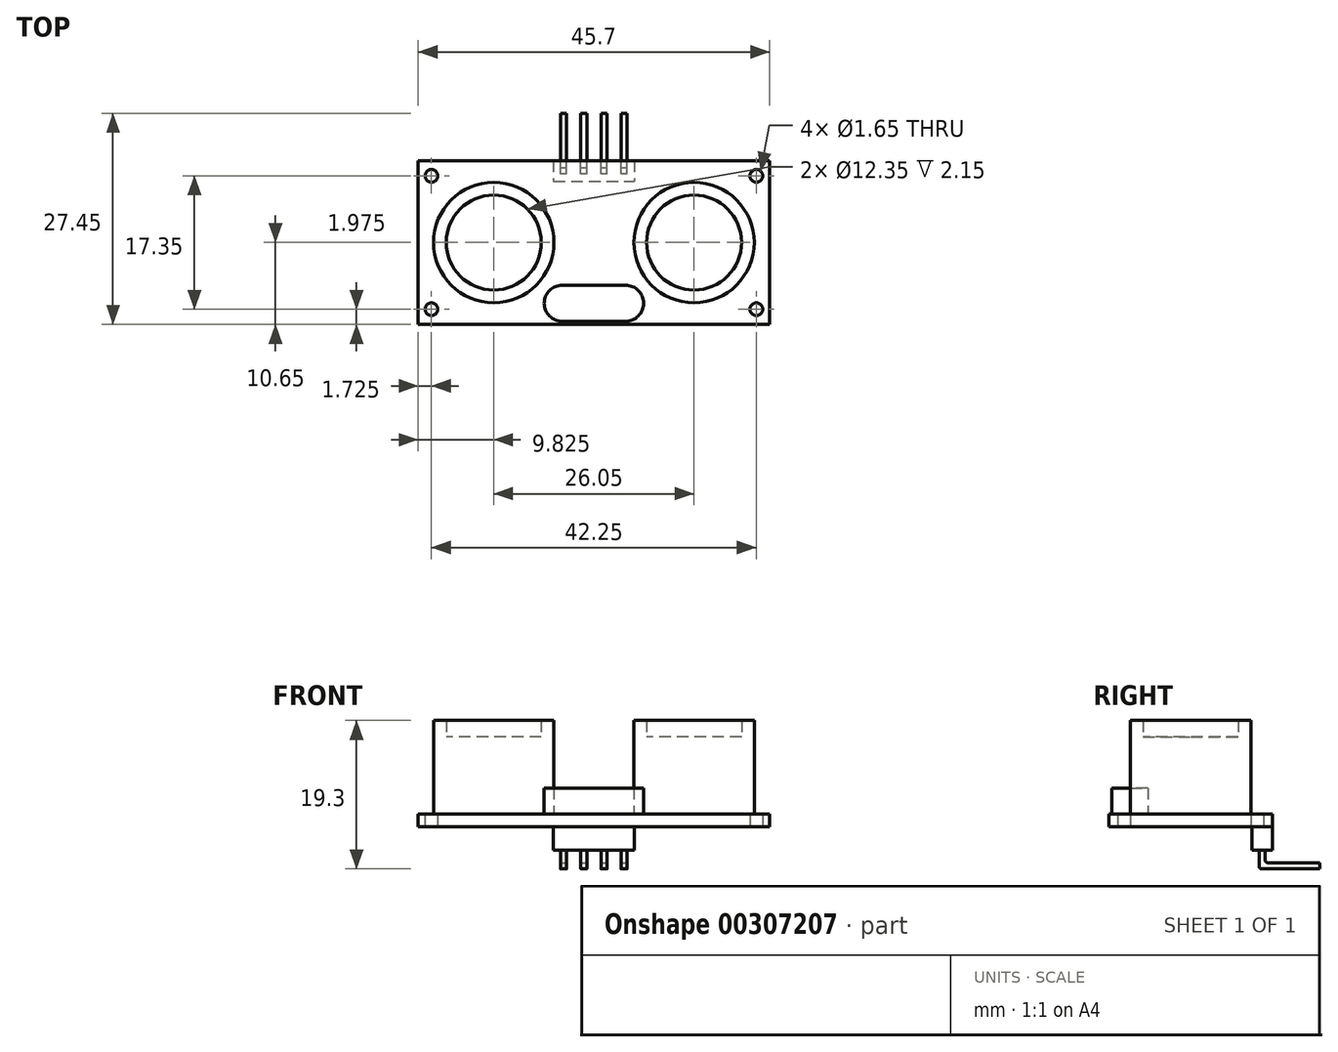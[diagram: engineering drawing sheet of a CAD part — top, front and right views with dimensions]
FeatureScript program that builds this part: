
annotation { "Feature Type Name" : "Feature", "Feature Type Description" : "" }
export const myFeature = defineFeature(function(context is Context, id is Id, definition is map)
    precondition{}
    {
        {
            var Q0;
            Q0=qCreatedBy(makeId("Top.planeOp"),FACE);
            var sketch = newSketch(context, id + "F0", { "sketchPlane" : qUnion([Q0])});
            skLineSegment(sketch, "E0.bottom", {"start": v(22.85, 10.65) * mm, "end": v(-22.85, 10.65) * mm});
            skLineSegment(sketch, "E0.top", {"start": v(22.85, -10.65) * mm, "end": v(-22.85, -10.65) * mm});
            skLineSegment(sketch, "E0.left", {"start": v(22.85, 10.65) * mm, "end": v(22.85, -10.65) * mm});
            skLineSegment(sketch, "E0.right", {"start": v(-22.85, 10.65) * mm, "end": v(-22.85, -10.65) * mm});
            skPoint(sketch, "E0.middle", {"position": v(0, 0) * mm});
            skCircle(sketch, "E1", {"center": v(-21.13, -8.68) * mm, "radius": 0.82 * mm});
            skCircle(sketch, "E2", {"center": v(-13.03, 0) * mm, "radius": 7.83 * mm});
            skCircle(sketch, "E3", {"center": v(13.03, 0) * mm, "radius": 7.83 * mm});
            skLineSegment(sketch, "E4", {"start": v(-22.85, 0) * mm, "end": v(-20.85, 0) * mm, "construction": true});
            skLineSegment(sketch, "E5", {"start": v(20.85, 0) * mm, "end": v(22.85, 0) * mm, "construction": true});
            skCircle(sketch, "E6.0", {"center": v(-13.03, 0) * mm, "radius": 6.17 * mm});
            skCircle(sketch, "E7.0", {"center": v(13.03, 0) * mm, "radius": 6.17 * mm});
            skLineSegment(sketch, "E8.bottom", {"start": v(-5.25, 10.65) * mm, "end": v(5.25, 10.65) * mm});
            skLineSegment(sketch, "E8.top", {"start": v(-5.25, 7.95) * mm, "end": v(5.25, 7.95) * mm});
            skLineSegment(sketch, "E8.left", {"start": v(-5.25, 10.65) * mm, "end": v(-5.25, 7.95) * mm});
            skLineSegment(sketch, "E8.right", {"start": v(5.25, 10.65) * mm, "end": v(5.25, 7.95) * mm});
            skPoint(sketch, "E9", {"position": v(0, 7.95) * mm});
            skLineSegment(sketch, "E10", {"start": v(-2.62, 7.95) * mm, "end": v(-2.63, 10.65) * mm});
            skLineSegment(sketch, "E11.1.0.0", {"start": v(0, 7.95) * mm, "end": v(0, 10.65) * mm});
            skLineSegment(sketch, "E11.2.0.0", {"start": v(2.63, 7.95) * mm, "end": v(2.62, 10.65) * mm});
            skLineSegment(sketch, "E11.direction1", {"start": v(-2.62, 7.95) * mm, "end": v(0, 7.95) * mm, "construction": true});
            skLineSegment(sketch, "E12", {"start": v(-5.25, 9.3) * mm, "end": v(-2.63, 9.3) * mm, "construction": true});
            skLineSegment(sketch, "E13", {"start": v(2.63, 9.3) * mm, "end": v(5.25, 9.3) * mm, "construction": true});
            skLineSegment(sketch, "E14", {"start": v(2.63, 9.3) * mm, "end": v(0, 9.3) * mm, "construction": true});
            skLineSegment(sketch, "E15", {"start": v(0, 9.3) * mm, "end": v(-2.63, 9.3) * mm, "construction": true});
            skCircle(sketch, "E16.0.1.0", {"center": v(-21.12, 8.68) * mm, "radius": 0.82 * mm});
            skCircle(sketch, "E16.1.0.0", {"center": v(21.12, -8.68) * mm, "radius": 0.82 * mm});
            skCircle(sketch, "E16.1.1.0", {"center": v(21.12, 8.68) * mm, "radius": 0.82 * mm});
            skLineSegment(sketch, "E16.direction1", {"start": v(-21.13, -8.67) * mm, "end": v(21.12, -8.67) * mm, "construction": true});
            skLineSegment(sketch, "E16.direction2", {"start": v(-21.13, -8.68) * mm, "end": v(-21.13, 8.68) * mm, "construction": true});
            skLineSegment(sketch, "E17", {"start": v(-4.11, -5.55) * mm, "end": v(4.11, -5.55) * mm});
            skPoint(sketch, "E18", {"position": v(0, -5.55) * mm});
            skLineSegment(sketch, "E19.0", {"start": v(-4.11, -10.25) * mm, "end": v(4.11, -10.25) * mm});
            skArc(sketch, "E20", {"start": v(4.11, -5.55) * mm, "mid": v(6.46, -7.9) * mm, "end": v(4.11, -10.25) * mm});
            skArc(sketch, "E21", {"start": v(-4.11, -5.55) * mm, "mid": v(-6.46, -7.9) * mm, "end": v(-4.11, -10.25) * mm});
            skSolve(sketch);
        }
        {
            var Q0;
            Q0=makeQuery(id+"F0.imprint","IMPRINT",FACE,{"disambiguationData":[TD([[makeQuery(id+"F0.imprint","IMPRINT",EDGE,{"derivedFrom":sQuery(id+"F0.wireOp",EDGE,"E0.bottom")}),1.0]])]});
            var Q1;
            {var subQ0=sQuery(id+"F0.wireOp",EDGE,"E8.left");Q1=makeQuery(id+"F0.imprint","IMPRINT",FACE,{"disambiguationData":[TD([[makeQuery(id+"F0.imprint","IMPRINT",EDGE,{"derivedFrom":subQ0}),1.0]])]});}
            var Q2;
            {var subQ0=sQuery(id+"F0.wireOp",EDGE,"E10");Q2=makeQuery(id+"F0.imprint","IMPRINT",FACE,{"disambiguationData":[TD([[makeQuery(id+"F0.imprint","IMPRINT",EDGE,{"derivedFrom":subQ0}),-1.0]])]});}
            var Q3;
            {var subQ0=sQuery(id+"F0.wireOp",EDGE,"E11.1.0.0");Q3=makeQuery(id+"F0.imprint","IMPRINT",FACE,{"disambiguationData":[TD([[makeQuery(id+"F0.imprint","IMPRINT",EDGE,{"derivedFrom":subQ0}),-1.0]])]});}
            var Q4;
            {var subQ0=sQuery(id+"F0.wireOp",EDGE,"E8.right");Q4=makeQuery(id+"F0.imprint","IMPRINT",FACE,{"disambiguationData":[TD([[makeQuery(id+"F0.imprint","IMPRINT",EDGE,{"derivedFrom":subQ0}),-1.0]])]});}
            extrude(context, id + "F1", {"entities" : qUnion([Q0, Q1, Q2, Q3, Q4]), "depth" : 1.6 * mm});
        }
        {
            var Q0;
            Q0=makeQuery(id+"F0.imprint","IMPRINT",FACE,{"disambiguationData":[TD([[makeQuery(id+"F0.imprint","IMPRINT",EDGE,{"derivedFrom":sQuery(id+"F0.wireOp",EDGE,"E3")}),1.0]])]});
            var Q1;
            Q1=makeQuery(id+"F0.imprint","IMPRINT",FACE,{"disambiguationData":[TD([[makeQuery(id+"F0.imprint","IMPRINT",EDGE,{"derivedFrom":sQuery(id+"F0.wireOp",EDGE,"E2")}),1.0]])]});
            extrude(context, id + "F2", {"entities" : qUnion([Q0, Q1]), "operationType" : NewBodyOperationType.ADD, "depth" : 13.8 * mm});
        }
        {
            var Q0;
            Q0=makeQuery(id+"F0.imprint","IMPRINT",FACE,{"disambiguationData":[TD([[makeQuery(id+"F0.imprint","IMPRINT",EDGE,{"derivedFrom":sQuery(id+"F0.wireOp",EDGE,"E6.0")}),1.0]])]});
            var Q1;
            Q1=makeQuery(id+"F0.imprint","IMPRINT",FACE,{"disambiguationData":[TD([[makeQuery(id+"F0.imprint","IMPRINT",EDGE,{"derivedFrom":sQuery(id+"F0.wireOp",EDGE,"E7.0")}),1.0]])]});
            extrude(context, id + "F3", {"entities" : qUnion([Q0, Q1]), "operationType" : NewBodyOperationType.ADD, "depth" : 11.65 * mm});
        }
        {
            var Q0;
            {var subQ0=sQuery(id+"F0.wireOp",EDGE,"E8.left");Q0=makeQuery(id+"F0.imprint","IMPRINT",FACE,{"disambiguationData":[TD([[makeQuery(id+"F0.imprint","IMPRINT",EDGE,{"derivedFrom":subQ0}),1.0]])]});}
            var Q1;
            {var subQ0=sQuery(id+"F0.wireOp",EDGE,"E10");Q1=makeQuery(id+"F0.imprint","IMPRINT",FACE,{"disambiguationData":[TD([[makeQuery(id+"F0.imprint","IMPRINT",EDGE,{"derivedFrom":subQ0}),-1.0]])]});}
            var Q2;
            {var subQ0=sQuery(id+"F0.wireOp",EDGE,"E11.1.0.0");Q2=makeQuery(id+"F0.imprint","IMPRINT",FACE,{"disambiguationData":[TD([[makeQuery(id+"F0.imprint","IMPRINT",EDGE,{"derivedFrom":subQ0}),-1.0]])]});}
            var Q3;
            {var subQ0=sQuery(id+"F0.wireOp",EDGE,"E8.right");Q3=makeQuery(id+"F0.imprint","IMPRINT",FACE,{"disambiguationData":[TD([[makeQuery(id+"F0.imprint","IMPRINT",EDGE,{"derivedFrom":subQ0}),-1.0]])]});}
            extrude(context, id + "F4", {"entities" : qUnion([Q0, Q1, Q2, Q3]), "oppositeDirection" : true, "depth" : 3.1 * mm});
        }
        {
            var Q0;
            Q0=makeQuery(id+"F4.opExtrude","CAP_FACE",FACE,{"disambiguationData":[OSD([sQuery(id+"F0.wireOp",EDGE,"E8.bottom"),sQuery(id+"F0.wireOp",EDGE,"E8.top"),sQuery(id+"F0.wireOp",EDGE,"E8.left"),sQuery(id+"F0.wireOp",EDGE,"E8.right")])],"isStart":false});
            var sketch = newSketch(context, id + "F5", { "sketchPlane" : qUnion([Q0])});
            skLineSegment(sketch, "E22.0.0", {"start": v(-5.25, -10.65) * mm, "end": v(5.25, -10.65) * mm});
            skLineSegment(sketch, "E22.0.1", {"start": v(5.25, -10.65) * mm, "end": v(5.25, -7.95) * mm});
            skLineSegment(sketch, "E22.0.2", {"start": v(5.25, -7.95) * mm, "end": v(-5.25, -7.95) * mm});
            skLineSegment(sketch, "E22.0.3", {"start": v(-5.25, -7.95) * mm, "end": v(-5.25, -10.65) * mm});
            skLineSegment(sketch, "E23.0", {"start": v(-5.25, -9.3) * mm, "end": v(-2.63, -9.3) * mm, "construction": true});
            skLineSegment(sketch, "E24.0", {"start": v(-2.62, -7.95) * mm, "end": v(-2.63, -10.65) * mm});
            skLineSegment(sketch, "E25.0", {"start": v(0, -9.3) * mm, "end": v(-2.63, -9.3) * mm, "construction": true});
            skLineSegment(sketch, "E26.0", {"start": v(0, -7.95) * mm, "end": v(0, -10.65) * mm});
            skLineSegment(sketch, "E27.0", {"start": v(2.63, -9.3) * mm, "end": v(0, -9.3) * mm, "construction": true});
            skLineSegment(sketch, "E28.0", {"start": v(2.63, -7.95) * mm, "end": v(2.62, -10.65) * mm});
            skLineSegment(sketch, "E29.0", {"start": v(2.63, -9.3) * mm, "end": v(5.25, -9.3) * mm, "construction": true});
            skPoint(sketch, "E30", {"position": v(-3.94, -9.3) * mm});
            skLineSegment(sketch, "E31.bottom", {"start": v(-3.54, -8.9) * mm, "end": v(-4.34, -8.9) * mm});
            skLineSegment(sketch, "E31.top", {"start": v(-3.54, -9.7) * mm, "end": v(-4.34, -9.7) * mm});
            skLineSegment(sketch, "E31.left", {"start": v(-3.54, -8.9) * mm, "end": v(-3.54, -9.7) * mm});
            skLineSegment(sketch, "E31.right", {"start": v(-4.34, -8.9) * mm, "end": v(-4.34, -9.7) * mm});
            skLineSegment(sketch, "E32", {"start": v(-4.34, -9.7) * mm, "end": v(-4.34, -16.8) * mm});
            skLineSegment(sketch, "E33", {"start": v(-3.54, -9.7) * mm, "end": v(-3.54, -16.8) * mm});
            skLineSegment(sketch, "E34", {"start": v(-4.34, -16.8) * mm, "end": v(-3.54, -16.8) * mm});
            skLineSegment(sketch, "E35.1.0.0", {"start": v(-0.91, -8.9) * mm, "end": v(-1.71, -8.9) * mm});
            skLineSegment(sketch, "E35.1.0.1", {"start": v(-1.71, -8.9) * mm, "end": v(-1.71, -9.7) * mm});
            skLineSegment(sketch, "E35.1.0.2", {"start": v(-0.91, -8.9) * mm, "end": v(-0.91, -9.7) * mm});
            skLineSegment(sketch, "E35.1.0.3", {"start": v(-0.91, -9.7) * mm, "end": v(-0.91, -16.8) * mm});
            skLineSegment(sketch, "E35.1.0.4", {"start": v(-1.71, -9.7) * mm, "end": v(-1.71, -16.8) * mm});
            skLineSegment(sketch, "E35.1.0.5", {"start": v(-0.91, -9.7) * mm, "end": v(-1.71, -9.7) * mm});
            skLineSegment(sketch, "E35.1.0.6", {"start": v(-1.71, -16.8) * mm, "end": v(-0.91, -16.8) * mm});
            skLineSegment(sketch, "E35.2.0.0", {"start": v(1.71, -8.9) * mm, "end": v(0.91, -8.9) * mm});
            skLineSegment(sketch, "E35.2.0.1", {"start": v(0.91, -8.9) * mm, "end": v(0.91, -9.7) * mm});
            skLineSegment(sketch, "E35.2.0.2", {"start": v(1.71, -8.9) * mm, "end": v(1.71, -9.7) * mm});
            skLineSegment(sketch, "E35.2.0.3", {"start": v(1.71, -9.7) * mm, "end": v(1.71, -16.8) * mm});
            skLineSegment(sketch, "E35.2.0.4", {"start": v(0.91, -9.7) * mm, "end": v(0.91, -16.8) * mm});
            skLineSegment(sketch, "E35.2.0.5", {"start": v(1.71, -9.7) * mm, "end": v(0.91, -9.7) * mm});
            skLineSegment(sketch, "E35.2.0.6", {"start": v(0.91, -16.8) * mm, "end": v(1.71, -16.8) * mm});
            skLineSegment(sketch, "E35.3.0.0", {"start": v(4.34, -8.9) * mm, "end": v(3.54, -8.9) * mm});
            skLineSegment(sketch, "E35.3.0.1", {"start": v(3.54, -8.9) * mm, "end": v(3.54, -9.7) * mm});
            skLineSegment(sketch, "E35.3.0.2", {"start": v(4.34, -8.9) * mm, "end": v(4.34, -9.7) * mm});
            skLineSegment(sketch, "E35.3.0.3", {"start": v(4.34, -9.7) * mm, "end": v(4.34, -16.8) * mm});
            skLineSegment(sketch, "E35.3.0.4", {"start": v(3.54, -9.7) * mm, "end": v(3.54, -16.8) * mm});
            skLineSegment(sketch, "E35.3.0.5", {"start": v(4.34, -9.7) * mm, "end": v(3.54, -9.7) * mm});
            skLineSegment(sketch, "E35.3.0.6", {"start": v(3.54, -16.8) * mm, "end": v(4.34, -16.8) * mm});
            skLineSegment(sketch, "E35.direction1", {"start": v(-4.34, -8.9) * mm, "end": v(-1.71, -8.9) * mm, "construction": true});
            skLineSegment(sketch, "E36", {"start": v(-5.25, -8.9) * mm, "end": v(-4.34, -8.9) * mm, "construction": true});
            skLineSegment(sketch, "E37", {"start": v(4.34, -8.9) * mm, "end": v(5.25, -8.9) * mm, "construction": true});
            skSolve(sketch);
        }
        {
            var Q0;
            Q0=makeQuery(id+"F5.imprint","IMPRINT",FACE,{"disambiguationData":[TD([[makeQuery(id+"F5.imprint","IMPRINT",EDGE,{"derivedFrom":sQuery(id+"F5.wireOp",EDGE,"E31.bottom")}),1.0]])]});
            var Q1;
            Q1=makeQuery(id+"F5.imprint","IMPRINT",FACE,{"disambiguationData":[TD([[makeQuery(id+"F5.imprint","IMPRINT",EDGE,{"derivedFrom":sQuery(id+"F5.wireOp",EDGE,"E35.1.0.0")}),1.0]])]});
            var Q2;
            Q2=makeQuery(id+"F5.imprint","IMPRINT",FACE,{"disambiguationData":[TD([[makeQuery(id+"F5.imprint","IMPRINT",EDGE,{"derivedFrom":sQuery(id+"F5.wireOp",EDGE,"E35.2.0.0")}),1.0]])]});
            var Q3;
            Q3=makeQuery(id+"F5.imprint","IMPRINT",FACE,{"disambiguationData":[TD([[makeQuery(id+"F5.imprint","IMPRINT",EDGE,{"derivedFrom":sQuery(id+"F5.wireOp",EDGE,"E35.3.0.0")}),1.0]])]});
            extrude(context, id + "F6", {"entities" : qUnion([Q0, Q1, Q2, Q3]), "operationType" : NewBodyOperationType.ADD, "depth" : 2.4 * mm});
        }
        {
            var Q0;
            Q0=makeQuery(id+"F6.opExtrude","CAP_FACE",FACE,{"disambiguationData":[OSD([sQuery(id+"F5.wireOp",EDGE,"E31.bottom"),sQuery(id+"F5.wireOp",EDGE,"E31.top"),sQuery(id+"F5.wireOp",EDGE,"E31.left"),sQuery(id+"F5.wireOp",EDGE,"E31.right")])],"isStart":false});
            var sketch = newSketch(context, id + "F7", { "sketchPlane" : qUnion([Q0])});
            skLineSegment(sketch, "E38.0", {"start": v(-4.34, -9.7) * mm, "end": v(-4.34, -16.8) * mm});
            skLineSegment(sketch, "E38.1", {"start": v(-3.54, -9.7) * mm, "end": v(-3.54, -16.8) * mm});
            skLineSegment(sketch, "E38.2", {"start": v(-1.71, -9.7) * mm, "end": v(-1.71, -16.8) * mm});
            skLineSegment(sketch, "E38.3", {"start": v(-0.91, -9.7) * mm, "end": v(-0.91, -16.8) * mm});
            skLineSegment(sketch, "E38.4", {"start": v(0.91, -9.7) * mm, "end": v(0.91, -16.8) * mm});
            skLineSegment(sketch, "E38.5", {"start": v(1.71, -9.7) * mm, "end": v(1.71, -16.8) * mm});
            skLineSegment(sketch, "E38.6", {"start": v(3.54, -9.7) * mm, "end": v(3.54, -16.8) * mm});
            skLineSegment(sketch, "E38.7", {"start": v(4.34, -9.7) * mm, "end": v(4.34, -16.8) * mm});
            skLineSegment(sketch, "E38.8", {"start": v(0.91, -16.8) * mm, "end": v(1.71, -16.8) * mm});
            skLineSegment(sketch, "E38.9", {"start": v(3.54, -16.8) * mm, "end": v(4.34, -16.8) * mm});
            skLineSegment(sketch, "E38.10", {"start": v(-1.71, -16.8) * mm, "end": v(-0.91, -16.8) * mm});
            skLineSegment(sketch, "E38.11", {"start": v(-4.34, -16.8) * mm, "end": v(-3.54, -16.8) * mm});
            skLineSegment(sketch, "E39", {"start": v(-4.34, -9.7) * mm, "end": v(-4.34, -8.9) * mm});
            skLineSegment(sketch, "E40", {"start": v(-4.34, -8.9) * mm, "end": v(-3.54, -8.9) * mm});
            skLineSegment(sketch, "E41", {"start": v(-3.54, -8.9) * mm, "end": v(-3.54, -9.7) * mm});
            skLineSegment(sketch, "E42", {"start": v(-1.71, -9.7) * mm, "end": v(-1.71, -8.9) * mm});
            skLineSegment(sketch, "E43", {"start": v(-1.71, -8.9) * mm, "end": v(-0.91, -8.9) * mm});
            skLineSegment(sketch, "E44", {"start": v(-0.91, -8.9) * mm, "end": v(-0.91, -9.7) * mm});
            skLineSegment(sketch, "E45", {"start": v(0.91, -9.7) * mm, "end": v(0.91, -8.9) * mm});
            skLineSegment(sketch, "E46", {"start": v(0.91, -8.9) * mm, "end": v(1.71, -8.9) * mm});
            skLineSegment(sketch, "E47", {"start": v(1.71, -8.9) * mm, "end": v(1.71, -9.7) * mm});
            skLineSegment(sketch, "E48", {"start": v(3.54, -9.7) * mm, "end": v(3.54, -8.9) * mm});
            skLineSegment(sketch, "E49", {"start": v(3.54, -8.9) * mm, "end": v(4.34, -8.9) * mm});
            skLineSegment(sketch, "E50", {"start": v(4.34, -8.9) * mm, "end": v(4.34, -9.7) * mm});
            skSolve(sketch);
        }
        {
            var Q0;
            Q0=qSketchRegion(id+"F7",true);
            extrude(context, id + "F8", {"entities" : qUnion([Q0]), "operationType" : NewBodyOperationType.ADD, "oppositeDirection" : true, "depth" : 0.8 * mm});
        }
        {
            var Q0;
            Q0=makeQuery(id+"F0.imprint","IMPRINT",FACE,{"disambiguationData":[TD([[makeQuery(id+"F0.imprint","IMPRINT",EDGE,{"derivedFrom":sQuery(id+"F0.wireOp",EDGE,"E17")}),-1.0]])]});
            extrude(context, id + "F9", {"entities" : qUnion([Q0]), "operationType" : NewBodyOperationType.ADD, "depth" : 5 * mm});
        }
        {
            var Q0;
            Q0=makeQuery(id+"F6.opExtrude","CAP_EDGE",EDGE,{"disambiguationData":[OSD([sQuery(id+"F5.wireOp",EDGE,"E31.bottom")])],"isStart":false});
            var Q1;
            Q1=makeQuery(id+"F6.opExtrude","CAP_EDGE",EDGE,{"disambiguationData":[OSD([sQuery(id+"F5.wireOp",EDGE,"E35.1.0.0")])],"isStart":false});
            var Q2;
            Q2=makeQuery(id+"F6.opExtrude","CAP_EDGE",EDGE,{"disambiguationData":[OSD([sQuery(id+"F5.wireOp",EDGE,"E35.2.0.0")])],"isStart":false});
            var Q3;
            Q3=makeQuery(id+"F6.opExtrude","CAP_EDGE",EDGE,{"disambiguationData":[OSD([sQuery(id+"F5.wireOp",EDGE,"E35.3.0.0")])],"isStart":false});
            var Q4;
            Q4=makeQuery(id+"F8.boolean.opBoolean","INTERSECT",EDGE,{"derivedFrom":[makeQuery(id+"F6.opExtrude","SWEPT_FACE",FACE,{"disambiguationData":[OSD([sQuery(id+"F5.wireOp",EDGE,"E35.3.0.5")])]}),makeQuery(id+"F8.opExtrude","CAP_FACE",FACE,{"disambiguationData":[OSD([sQuery(id+"F7.wireOp",EDGE,"E38.6"),sQuery(id+"F7.wireOp",EDGE,"E38.7"),sQuery(id+"F7.wireOp",EDGE,"E38.9"),sQuery(id+"F7.wireOp",EDGE,"E48"),sQuery(id+"F7.wireOp",EDGE,"E49"),sQuery(id+"F7.wireOp",EDGE,"E50")])],"isStart":false})]});
            var Q5;
            Q5=makeQuery(id+"F8.boolean.opBoolean","INTERSECT",EDGE,{"derivedFrom":[makeQuery(id+"F6.opExtrude","SWEPT_FACE",FACE,{"disambiguationData":[OSD([sQuery(id+"F5.wireOp",EDGE,"E35.2.0.5")])]}),makeQuery(id+"F8.opExtrude","CAP_FACE",FACE,{"disambiguationData":[OSD([sQuery(id+"F7.wireOp",EDGE,"E38.4"),sQuery(id+"F7.wireOp",EDGE,"E38.5"),sQuery(id+"F7.wireOp",EDGE,"E38.8"),sQuery(id+"F7.wireOp",EDGE,"E45"),sQuery(id+"F7.wireOp",EDGE,"E46"),sQuery(id+"F7.wireOp",EDGE,"E47")])],"isStart":false})]});
            var Q6;
            Q6=makeQuery(id+"F8.boolean.opBoolean","INTERSECT",EDGE,{"derivedFrom":[makeQuery(id+"F6.opExtrude","SWEPT_FACE",FACE,{"disambiguationData":[OSD([sQuery(id+"F5.wireOp",EDGE,"E35.1.0.5")])]}),makeQuery(id+"F8.opExtrude","CAP_FACE",FACE,{"disambiguationData":[OSD([sQuery(id+"F7.wireOp",EDGE,"E38.2"),sQuery(id+"F7.wireOp",EDGE,"E38.3"),sQuery(id+"F7.wireOp",EDGE,"E38.10"),sQuery(id+"F7.wireOp",EDGE,"E42"),sQuery(id+"F7.wireOp",EDGE,"E43"),sQuery(id+"F7.wireOp",EDGE,"E44")])],"isStart":false})]});
            var Q7;
            Q7=makeQuery(id+"F8.boolean.opBoolean","INTERSECT",EDGE,{"derivedFrom":[makeQuery(id+"F6.opExtrude","SWEPT_FACE",FACE,{"disambiguationData":[OSD([sQuery(id+"F5.wireOp",EDGE,"E31.top")])]}),makeQuery(id+"F8.opExtrude","CAP_FACE",FACE,{"disambiguationData":[OSD([sQuery(id+"F7.wireOp",EDGE,"E38.0"),sQuery(id+"F7.wireOp",EDGE,"E38.1"),sQuery(id+"F7.wireOp",EDGE,"E38.11"),sQuery(id+"F7.wireOp",EDGE,"E39"),sQuery(id+"F7.wireOp",EDGE,"E40"),sQuery(id+"F7.wireOp",EDGE,"E41")])],"isStart":false})]});
            fillet(context, id + "F10", {"entities" : qUnion([Q0, Q1, Q2, Q3, Q4, Q5, Q6, Q7]), "radius" : 0.3 * mm, "tangentPropagation" : true, "allowEdgeOverflow" : false});
        }
    });
